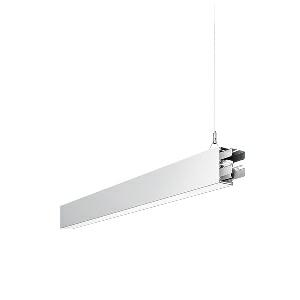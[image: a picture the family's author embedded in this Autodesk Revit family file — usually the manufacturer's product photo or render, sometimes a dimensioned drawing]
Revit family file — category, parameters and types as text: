
# Revit family: dotoo_line_-_dlp_1500_840_d_mid_00805778_8f54
name_source: partatom
category: Lighting Fixtures
units: mm (PartAtom-declared; Revit-internal decimal feet)

## family parameters
Cut with Voids When Loaded = No
Host = Face
Light Source = No
Part Type = Normal
Room Calculation Point = No
Round Connector Dimension = Use Diameter
Shared = No

## types (1)
- DOTOO.line - DLP 1500/840/D MID (1 x LED, 1350 lm, 4000K)
    Apparent Load = 13 VA
    Approval mark = CE
    CIE Flux Codes = 67 91 98 100 100
    Color Rendering = 80-89
    Color Temperature = 4000K
    Control Gear = Electronic ballast
    Default Elevation = 1800 mm
    Description = DLP 1500/840/D|Suspended luminaire|light source: LED|connected load: 220-240 V, 50/60 Hz|Power consumption: approx. 13 W|standby: approx. 0,20|luminous flux: 1350 lm|luminous efficacy: 103 lm/W|light distribution: Direct|direct ratio: approx. 100 %|colour temperature: Cold white, ca. 4000 K|color rendering index (CRI): >= 80|chromaticity tolerance:  3 SDCM|System of protection: IP 40|technology: Continuously dimmable|luminaire body|material: Sectional aluminium|colour: White|lamp cover: Acrylic (PMMA), Clear|mains lead: 1,0 m With free stranded wires|Fastening: Steel cable 0.3 - 0.7 m|glare control: Prism aperture|luminance(L65): <= 3000 cd/m|unified glare rating(4H 8H): <=  19|special features: DALI Load 1x, TouchDIM - dimming via standard switch, Through-wired, up to 18 m on one mains connection, Flicker-free, Suitable as emergency lighting, Mechanical and electrical connection of the individual modules without tools|
    Frequency = 50 Hz
    Height = 110 mm
    Lamp = 1 x LED
    Lamp Light Flux = 1350 lm
    Lamp count = 1
    Length = 1122 mm
    Luminous efficacy = 104 lm/W
    Manufacturer = Waldmann
    ModVariant = No
    Model = 00805778
    Mounting Place = Ceiling
    Mounting Type = Pendant
    Number of Poles = 1
    OnlyDefault = Yes
    Power Factor = 1
    Product Name = DOTOO.line - DLP 1500/840/D MID
    Product group = Suspended luminaire
    ProductGroupID = 9
    Protection Class = Protection class I
    Protection Degree = IP 40
    RLX_Detail_Level = 1
    RLX_Emergency_Light_Flux = 0 lm
    RLX_Emergency_Type = 0
    RLX_Emergency_Type_DB = No
    RlxData = <blob elided: 19505 chars, md5=4531c62b>
    Socket = socket
    Standby Power = 0 W
    System Light Flux = 1350 lm
    System Power = 13 W
    Type Comments = Product without accessories
    Type Image = 113302000-00692570.jpg
    URL = http://relux.com
    VarID = ---
    Voltage = 230 V
    Voltage Range = 220-240 V
    Weight = 0.00 kg
    Width = 60 mm  [stored 0.19685 ft]

note: [stored X ft] marks values corroborated as IEEE doubles in the binary element streams (Revit-internal decimal feet)

## geometry (parser evidence)
native form markers: Blend x4, Sweep x12
no freeform markers — native parametric forms only
